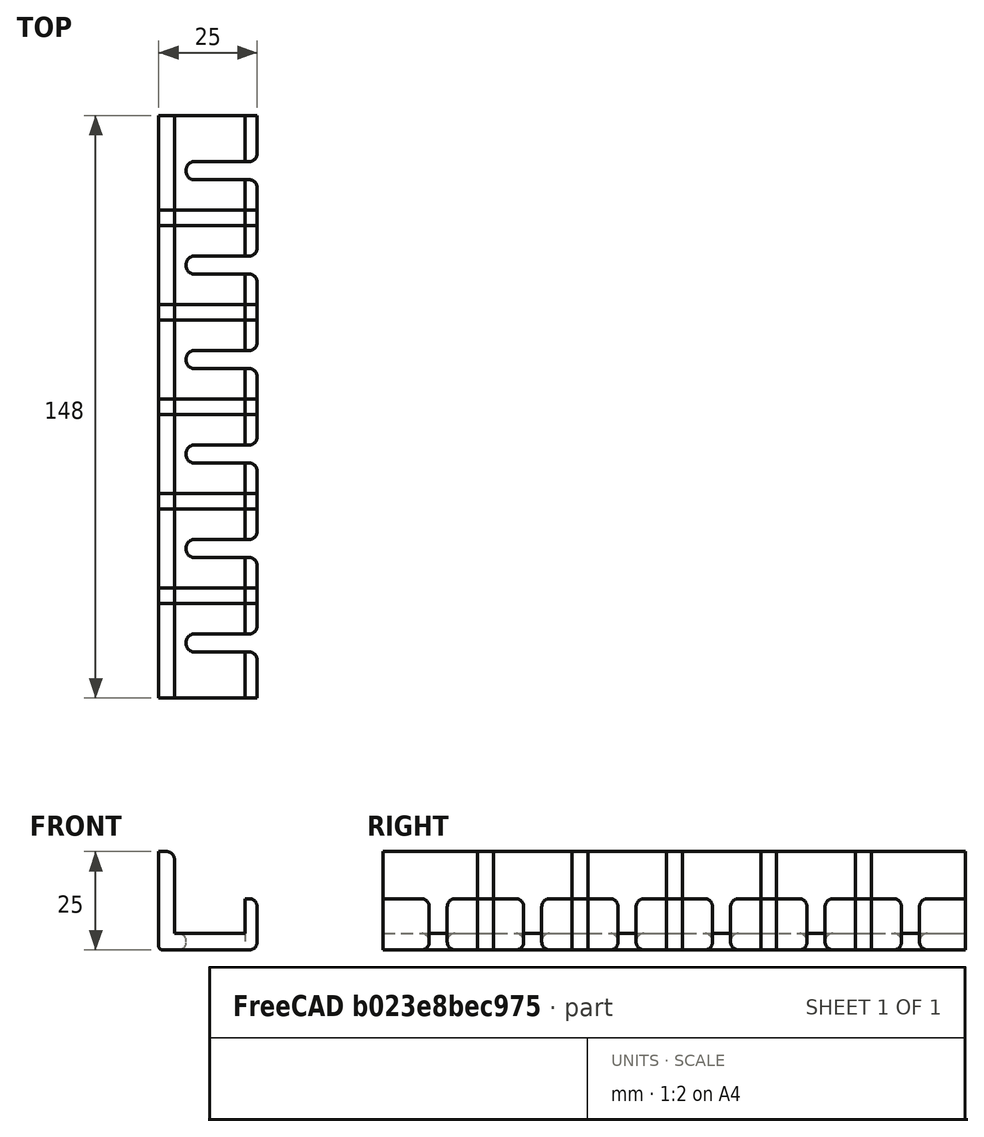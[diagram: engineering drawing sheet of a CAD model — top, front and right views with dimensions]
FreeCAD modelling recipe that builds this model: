
FCSTD DOCUMENT  (FreeCAD 0.19R24267 +148 (Git))
Label: 2_cables
License: All rights reserved
LicenseURL: http://en.wikipedia.org/wiki/All_rights_reserved
objects: Part::Fillet×6, Part::Feature×6, Part::Box×4, Part::Cut×2, Part::MultiFuse×1
note: 19 computed .brp shape members not serialized (recipe doc carries the construction recipe); baked Part::Feature solids carry a one-line shape summary decoded from their .brp

FEATURE [Part::Box] Box  label="Cube"
  AttacherType = Attacher::AttachEngine3D
  Height = 25
  Length = 25
  Placement = pos=(0,-14,0) rot=(0,0,1;0rad)
  Width = 28
FEATURE [Part::Box] Box001  label="Cube001"
  AttacherType = Attacher::AttachEngine3D
  Height = 25
  Length = 18
  Placement = pos=(4,-16,4.2) rot=(0,0,1;0rad)
  Width = 32
FEATURE [Part::Box] Box002  label="Cube002"
  AttacherType = Attacher::AttachEngine3D
  Height = 13
  Length = 18
  Placement = pos=(10,-16,13) rot=(0,0,1;0rad)
  Width = 32
FEATURE [Part::MultiFuse] Fusion
  Shapes = -> [Box001,Box002]
FEATURE [Part::Box] Box003  label="Cube003"
  AttacherType = Attacher::AttachEngine3D
  Height = 30
  Length = 30
  Placement = pos=(7,-2.3,0) rot=(0,0,1;0rad)
  Width = 4.6
FEATURE [Part::Fillet] Fillet001  label="CableCut"
  Base = -> Box003
  Edges = 2 edges r=2: [Edge1,Edge3]
FEATURE [Part::Cut] Cut
  Base = -> Box
  Tool = -> Fusion
FEATURE [Part::Fillet] Fillet
  Base = -> Cut
  Edges = 2 edges r=2: [Edge13,Edge21]
FEATURE [Part::Cut] Cut001
  Base = -> Fillet
  Tool = -> Fillet001
FEATURE [Part::Fillet] Fillet002
  Base = -> Cut001
  Edges = 1 edges r=2: [Edge36]
FEATURE [Part::Fillet] Fillet003
  Base = -> Fillet002
  Edges = 2 edges r=2: [Edge54,Edge59]
FEATURE [Part::Fillet] Fillet004
  Base = -> Fillet003
  Edges = 1 edges r=2: [Edge61]
FEATURE [Part::Fillet] Fillet005
  Base = -> Fillet004
  Edges = 1 edges r=1: [Edge40]
FEATURE [Part::Feature] Fillet005001001  label="Segment001"
  shape: bbox 25 x 28 x 25 mm, 42 faces (baked)
FEATURE [Part::Feature] Fillet005001002  label="Segment002"
  Placement = pos=(0,24,0) rot=(0,0,1;0rad)
  shape: bbox 25 x 28 x 25 mm, 42 faces (baked)
FEATURE [Part::Feature] Fillet005001003  label="Segment003"
  Placement = pos=(0,48,0) rot=(0,0,1;0rad)
  shape: bbox 25 x 28 x 25 mm, 42 faces (baked)
FEATURE [Part::Feature] Fillet005001004  label="Segment004"
  Placement = pos=(0,72,0) rot=(0,0,1;0rad)
  shape: bbox 25 x 28 x 25 mm, 42 faces (baked)
FEATURE [Part::Feature] Fillet005001005  label="Segment005"
  Placement = pos=(0,96,0) rot=(0,0,1;0rad)
  shape: bbox 25 x 28 x 25 mm, 42 faces (baked)
FEATURE [Part::Feature] Fillet005001006  label="Segment006"
  Placement = pos=(0,120,0) rot=(0,0,1;0rad)
  shape: bbox 25 x 28 x 25 mm, 42 faces (baked)
